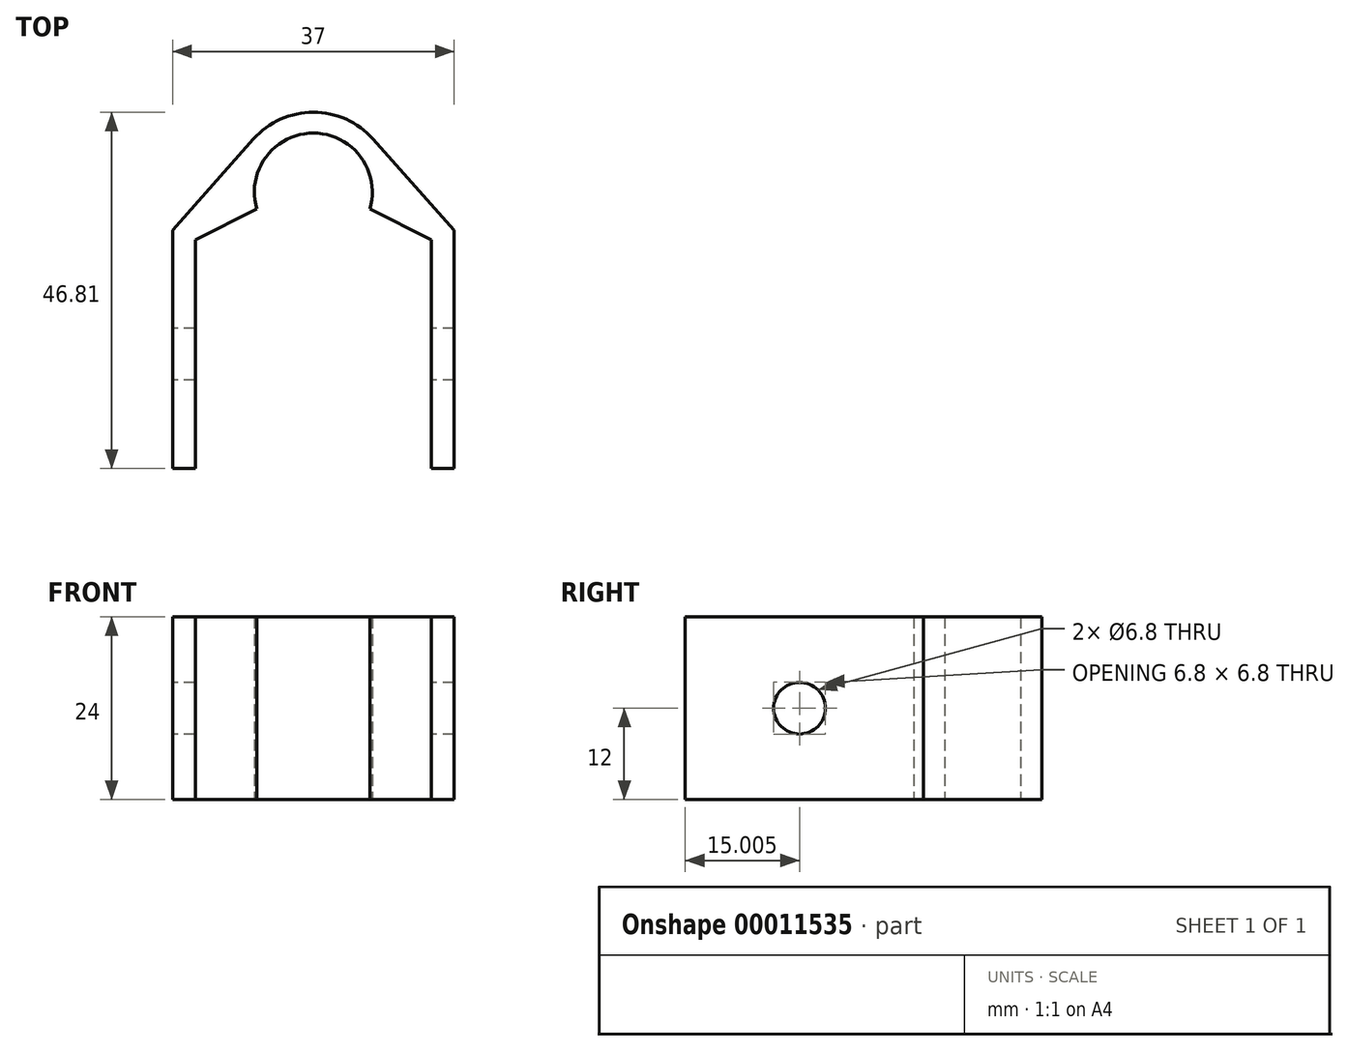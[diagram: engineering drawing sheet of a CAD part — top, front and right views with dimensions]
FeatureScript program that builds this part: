
annotation { "Feature Type Name" : "Feature", "Feature Type Description" : "" }
export const myFeature = defineFeature(function(context is Context, id is Id, definition is map)
    precondition{}
    {
        {
            var Q0;
            Q0=qCreatedBy(makeId("Top.planeOp"),FACE);
            var sketch = newSketch(context, id + "F0", { "sketchPlane" : qUnion([Q0])});
            skLineSegment(sketch, "E0", {"start": v(-15.5, 4.88) * mm, "end": v(-15.5, -25.12) * mm});
            skLineSegment(sketch, "E1", {"start": v(15.5, 4.88) * mm, "end": v(15.5, -25.12) * mm});
            skLineSegment(sketch, "E2", {"start": v(15.5, 4.88) * mm, "end": v(7.42, 8.97) * mm});
            skLineSegment(sketch, "E3", {"start": v(-15.5, 4.88) * mm, "end": v(-7.42, 8.97) * mm});
            skArc(sketch, "E4", {"start": v(7.42, 8.97) * mm, "mid": v(0, 18.94) * mm, "end": v(-7.42, 8.97) * mm});
            skArc(sketch, "E5", {"start": v(7.85, 18.17) * mm, "mid": v(0, 21.69) * mm, "end": v(-7.85, 18.17) * mm});
            skLineSegment(sketch, "E6", {"start": v(18.5, -25.12) * mm, "end": v(18.5, 6.19) * mm});
            skLineSegment(sketch, "E7", {"start": v(-18.5, -25.12) * mm, "end": v(-18.5, 6.19) * mm});
            skLineSegment(sketch, "E8", {"start": v(18.5, 6.19) * mm, "end": v(7.85, 18.17) * mm});
            skLineSegment(sketch, "E9", {"start": v(-18.5, 6.19) * mm, "end": v(-7.85, 18.17) * mm});
            skLineSegment(sketch, "E10", {"start": v(15.5, -25.12) * mm, "end": v(18.5, -25.12) * mm});
            skLineSegment(sketch, "E11", {"start": v(-15.5, -25.12) * mm, "end": v(-18.5, -25.12) * mm});
            skSolve(sketch);
        }
        {
            var Q0;
            Q0=makeQuery(id+"F0.imprint","IMPRINT",FACE,{"disambiguationData":[TD([[makeQuery(id+"F0.imprint","IMPRINT",EDGE,{"derivedFrom":sQuery(id+"F0.wireOp",EDGE,"E0")}),-1.0]])]});
            extrude(context, id + "F1", {"entities" : qUnion([Q0]), "depth" : 24 * mm});
        }
        {
            var Q0;
            Q0=makeQuery(id+"F1.opExtrude","SWEPT_FACE",FACE,{"disambiguationData":[OSD([sQuery(id+"F0.wireOp",EDGE,"E7")])]});
            var sketch = newSketch(context, id + "F2", { "sketchPlane" : qUnion([Q0])});
            skCircle(sketch, "E12", {"center": v(10.12, 12) * mm, "radius": 3.4 * mm});
            skSolve(sketch);
        }
        {
            var Q0;
            Q0=makeQuery(id+"F2.imprint","IMPRINT",FACE,{"disambiguationData":[TD([[makeQuery(id+"F2.imprint","IMPRINT",EDGE,{"derivedFrom":sQuery(id+"F2.wireOp",EDGE,"E12")}),1.0]])]});
            extrude(context, id + "F3", {"entities" : qUnion([Q0]), "operationType" : NewBodyOperationType.REMOVE, "endBound" : BoundingType.THROUGH_ALL, "oppositeDirection" : true, "depth" : 25 * mm});
        }
    });
